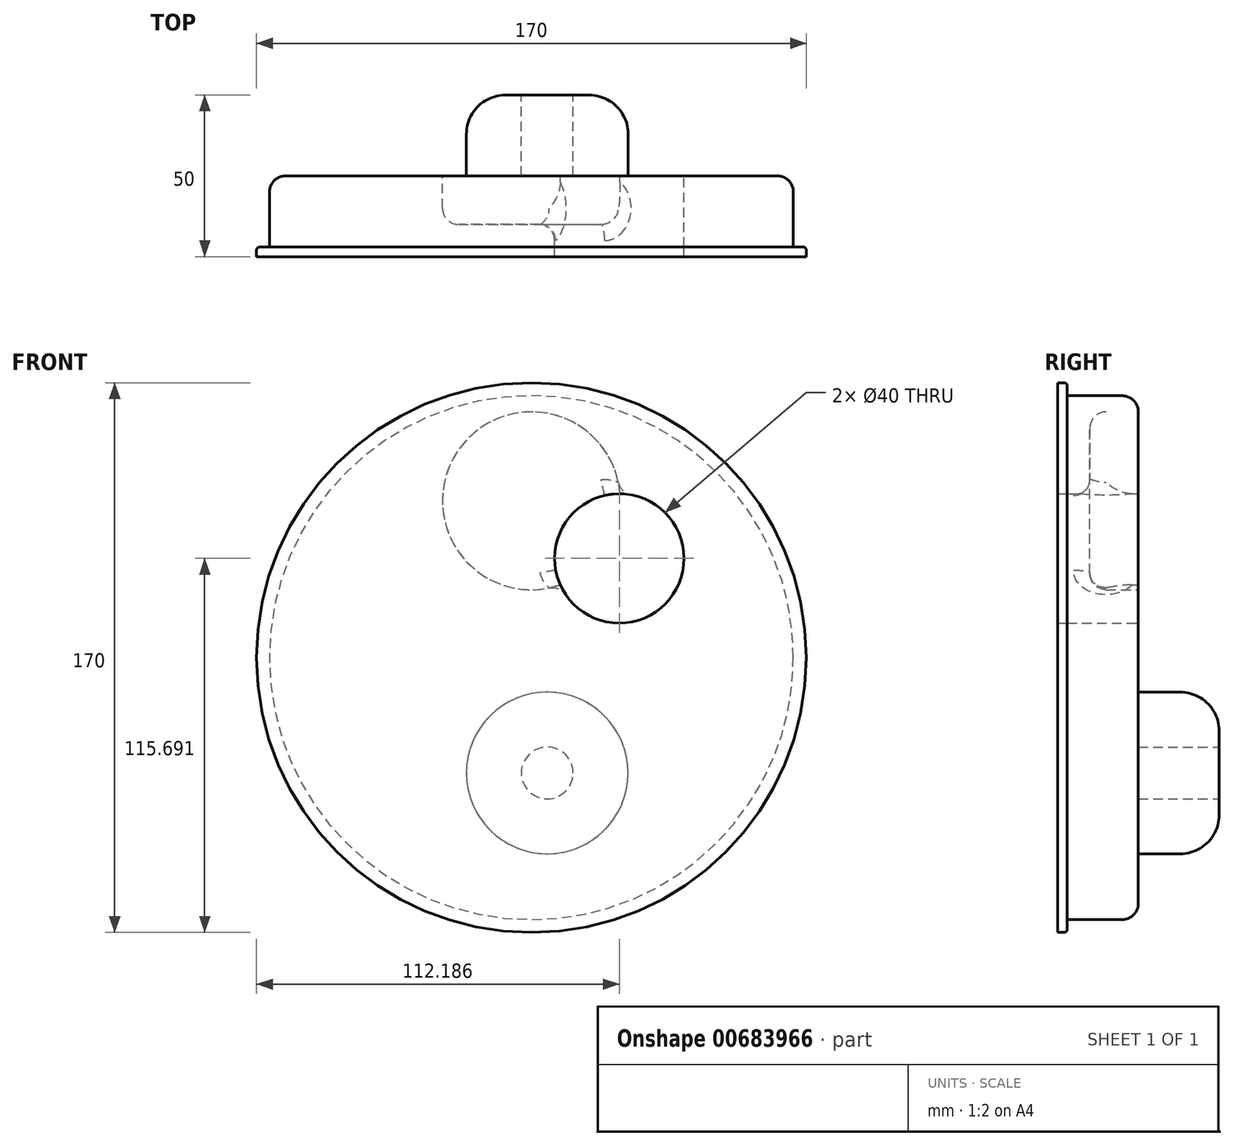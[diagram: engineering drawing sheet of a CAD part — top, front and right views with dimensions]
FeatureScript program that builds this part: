
annotation { "Feature Type Name" : "Feature", "Feature Type Description" : "" }
export const myFeature = defineFeature(function(context is Context, id is Id, definition is map)
    precondition{}
    {
        {
            var Q0;
            Q0=qCreatedBy(makeId("Front.planeOp"),FACE);
            var sketch = newSketch(context, id + "F0", { "sketchPlane" : qUnion([Q0])});
            skCircle(sketch, "E0", {"center": v(0, 0) * mm, "radius": 85 * mm});
            skSolve(sketch);
        }
        {
            var Q0;
            Q0=makeQuery(id+"F0.imprint","IMPRINT",FACE,{"disambiguationData":[TD([[makeQuery(id+"F0.imprint","IMPRINT",EDGE,{"derivedFrom":sQuery(id+"F0.wireOp",EDGE,"E0")}),1.0]])]});
            var Q1;
            Q1=sQuery(id+"F0.wireOp",EDGE,"E0");
            extrude(context, id + "F1", {"entities" : qUnion([Q0]), "surfaceEntities" : qUnion([Q1]), "depth" : 3 * mm, "offsetDistance" : 25 * mm});
        }
        {
            var Q0;
            Q0=qCreatedBy(makeId("Front.planeOp"),FACE);
            var sketch = newSketch(context, id + "F2", { "sketchPlane" : qUnion([Q0])});
            skCircle(sketch, "E1", {"center": v(0, 0) * mm, "radius": 75 * mm});
            skSolve(sketch);
        }
        {
            var Q0;
            Q0=makeQuery(id+"F2.imprint","IMPRINT",FACE,{"disambiguationData":[TD([[makeQuery(id+"F2.imprint","IMPRINT",EDGE,{"derivedFrom":sQuery(id+"F2.wireOp",EDGE,"E1")}),1.0]])]});
            var Q1;
            Q1=sQuery(id+"F2.wireOp",EDGE,"E1");
            extrude(context, id + "F3", {"entities" : qUnion([Q0]), "bodyType" : ToolBodyType.SURFACE, "surfaceEntities" : qUnion([Q1]), "depth" : 11 * mm, "offsetDistance" : 25 * mm});
        }
        {
            var Q0;
            Q0=makeQuery(id+"F1.opExtrude","CAP_EDGE",EDGE,{"disambiguationData":[OSD([sQuery(id+"F0.wireOp",EDGE,"E0")])],"isStart":true});
            fillet(context, id + "F4", {"entities" : qUnion([Q0]), "radius" : 1 * mm, "tangentPropagation" : true, "allowEdgeOverflow" : false});
        }
        {
            var Q0;
            Q0=qCreatedBy(makeId("Front.planeOp"),FACE);
            var sketch = newSketch(context, id + "F5", { "sketchPlane" : qUnion([Q0])});
            skCircle(sketch, "E2", {"center": v(0, 0) * mm, "radius": 81 * mm});
            skSolve(sketch);
        }
        {
            var Q0;
            Q0=makeQuery(id+"F5.imprint","IMPRINT",FACE,{"disambiguationData":[TD([[makeQuery(id+"F5.imprint","IMPRINT",EDGE,{"derivedFrom":sQuery(id+"F5.wireOp",EDGE,"E2")}),1.0]])]});
            var Q1;
            Q1=sQuery(id+"F5.wireOp",EDGE,"E2");
            extrude(context, id + "F6", {"entities" : qUnion([Q0]), "surfaceEntities" : qUnion([Q1]), "oppositeDirection" : true, "depth" : 22 * mm, "offsetDistance" : 25 * mm});
        }
        {
            var Q0;
            Q0=makeQuery(id+"F6.opExtrude","CAP_EDGE",EDGE,{"disambiguationData":[OSD([sQuery(id+"F5.wireOp",EDGE,"E2")])],"isStart":false});
            fillet(context, id + "F7", {"entities" : qUnion([Q0]), "radius" : 5 * mm, "tangentPropagation" : true, "allowEdgeOverflow" : false});
        }
        {
            var Q0;
            Q0=makeQuery(id+"F6.opExtrude","CAP_FACE",FACE,{"disambiguationData":[OSD([sQuery(id+"F5.wireOp",EDGE,"E2")])],"isStart":false});
            var sketch = newSketch(context, id + "F8", { "sketchPlane" : qUnion([Q0])});
            skCircle(sketch, "E3", {"center": v(0, 48.5) * mm, "radius": 27.5 * mm});
            skCircle(sketch, "E4", {"center": v(-27.19, 30.7) * mm, "radius": 20 * mm});
            skLineSegment(sketch, "E5", {"start": v(9.35, 22.64) * mm, "end": v(-20.38, 11.88) * mm});
            skLineSegment(sketch, "E6", {"start": v(-19.97, 67.4) * mm, "end": v(-41.71, 44.44) * mm});
            skSolve(sketch);
        }
        {
            var Q0;
            {var subQ0=sQuery(id+"F8.wireOp",EDGE,"E4");var subQ1=sQuery(id+"F8.wireOp",EDGE,"E3");var subQ2=makeQuery(id+"F8.imprint","INTERSECT",VERTEX,{"disambiguationData":[OD(0.0)],"derivedFrom":[subQ1,subQ0]});Q0=makeQuery(id+"F8.imprint","IMPRINT",FACE,{"disambiguationData":[TD([[makeQuery(id+"F8.imprint","IMPRINT",EDGE,{"disambiguationData":[TD([[subQ2,-1.0]])],"derivedFrom":subQ1}),1.0]])]});}
            var Q1;
            {var subQ0=sQuery(id+"F8.wireOp",EDGE,"E4");var subQ1=sQuery(id+"F8.wireOp",EDGE,"E3");var subQ2=makeQuery(id+"F8.imprint","INTERSECT",VERTEX,{"disambiguationData":[OD(0.0)],"derivedFrom":[subQ1,subQ0]});Q1=makeQuery(id+"F8.imprint","IMPRINT",FACE,{"disambiguationData":[TD([[makeQuery(id+"F8.imprint","IMPRINT",EDGE,{"disambiguationData":[TD([[subQ2,-1.0]])],"derivedFrom":subQ1}),-1.0]])]});}
            extrude(context, id + "F9", {"entities" : qUnion([Q0, Q1]), "operationType" : NewBodyOperationType.REMOVE, "oppositeDirection" : true, "depth" : 55 * mm, "offsetDistance" : 25 * mm});
        }
        {
            var Q0;
            Q0=qCreatedBy(makeId("Front.planeOp"),FACE);
            var sketch = newSketch(context, id + "F10", { "sketchPlane" : qUnion([Q0])});
            skCircle(sketch, "E7", {"center": v(27.19, 30.7) * mm, "radius": 20 * mm});
            skSolve(sketch);
        }
        {
            var Q0;
            Q0 = qSketchRegion(id + "F10", true);
            extrude(context, id + "F11", {"entities" : qUnion([Q0]), "operationType" : NewBodyOperationType.REMOVE, "depth" : 25 * mm, "offsetDistance" : 25 * mm});
        }
        {
            var Q0;
            {var subQ0=sQuery(id+"F8.wireOp",EDGE,"E3");var subQ6=makeQuery(id+"F8.imprint","INTERSECT",VERTEX,{"derivedFrom":[subQ0,sQuery(id+"F8.wireOp",EDGE,"E6")]});Q0=makeQuery(id+"F8.imprint","IMPRINT",FACE,{"disambiguationData":[TD([[makeQuery(id+"F8.imprint","IMPRINT",EDGE,{"disambiguationData":[TD([[subQ6,-1.0]])],"derivedFrom":subQ0}),1.0]])]});}
            var Q1;
            {var subQ0=sQuery(id+"F8.wireOp",EDGE,"E4");var subQ1=sQuery(id+"F8.wireOp",EDGE,"E3");var subQ2=makeQuery(id+"F8.imprint","INTERSECT",VERTEX,{"disambiguationData":[OD(0.0)],"derivedFrom":[subQ1,subQ0]});Q1=makeQuery(id+"F8.imprint","IMPRINT",FACE,{"disambiguationData":[TD([[makeQuery(id+"F8.imprint","IMPRINT",EDGE,{"disambiguationData":[TD([[subQ2,-1.0]])],"derivedFrom":subQ1}),1.0]])]});}
            var Q2;
            Q2=sQuery(id+"F8.wireOp",EDGE,"E3");
            extrude(context, id + "F12", {"entities" : qUnion([Q0, Q1]), "operationType" : NewBodyOperationType.REMOVE, "surfaceEntities" : qUnion([Q2]), "oppositeDirection" : true, "depth" : 15 * mm, "offsetDistance" : 25 * mm});
        }
        {
            var Q0;
            Q0=makeQuery(id+"F12.boolean.opBoolean","COPY",EDGE,{"derivedFrom":makeQuery(id+"F12.opExtrude","CAP_EDGE",EDGE,{"disambiguationData":[OSD([sQuery(id+"F8.wireOp",EDGE,"E3")])],"isStart":false})});
            var Q1;
            Q1=makeQuery(id+"F12.boolean.opBoolean","INTERSECT",EDGE,{"derivedFrom":[makeQuery(id+"F9.boolean.opBoolean","COPY",FACE,{"derivedFrom":makeQuery(id+"F9.opExtrude","SWEPT_FACE",FACE,{"disambiguationData":[OSD([sQuery(id+"F8.wireOp",EDGE,"E4")])]})}),makeQuery(id+"F12.opExtrude","CAP_FACE",FACE,{"disambiguationData":[OSD([sQuery(id+"F8.wireOp",EDGE,"E3")])],"isStart":false})]});
            fillet(context, id + "F13", {"entities" : qUnion([Q0, Q1]), "radius" : 5 * mm, "tangentPropagation" : true, "allowEdgeOverflow" : false});
        }
        {
            var Q0;
            {var subQ0=sQuery(id+"F8.wireOp",EDGE,"E5");Q0=makeQuery(id+"F8.imprint","IMPRINT",FACE,{"disambiguationData":[TD([[makeQuery(id+"F8.imprint","IMPRINT",EDGE,{"derivedFrom":subQ0}),1.0]])]});}
            var sketch = newSketch(context, id + "F14", { "sketchPlane" : qUnion([Q0])});
            skCircle(sketch, "E8", {"center": v(-4.9, -35.67) * mm, "radius": 25 * mm});
            skSolve(sketch);
        }
        {
            var Q0;
            Q0 = qSketchRegion(id + "F14", true);
            extrude(context, id + "F15", {"entities" : qUnion([Q0]), "operationType" : NewBodyOperationType.ADD, "depth" : 25 * mm, "offsetDistance" : 25 * mm});
        }
        {
            var Q0;
            Q0=makeQuery(id+"F15.opExtrude","CAP_EDGE",EDGE,{"disambiguationData":[OSD([sQuery(id+"F14.wireOp",EDGE,"E8")])],"isStart":false});
            fillet(context, id + "F16", {"entities" : qUnion([Q0]), "radius" : 12.07 * mm, "tangentPropagation" : true, "allowEdgeOverflow" : false});
        }
        {
            var Q0;
            Q0=makeQuery(id+"F15.opExtrude","CAP_FACE",FACE,{"disambiguationData":[OSD([sQuery(id+"F14.wireOp",EDGE,"E8")])],"isStart":false});
            var sketch = newSketch(context, id + "F17", { "sketchPlane" : qUnion([Q0])});
            skCircle(sketch, "E9", {"center": v(-4.9, -35.67) * mm, "radius": 8 * mm});
            skSolve(sketch);
        }
        {
            var Q0;
            Q0 = qSketchRegion(id + "F17", true);
            extrude(context, id + "F18", {"entities" : qUnion([Q0]), "operationType" : NewBodyOperationType.REMOVE, "oppositeDirection" : true, "depth" : 25 * mm, "offsetDistance" : 25 * mm});
        }
    });
